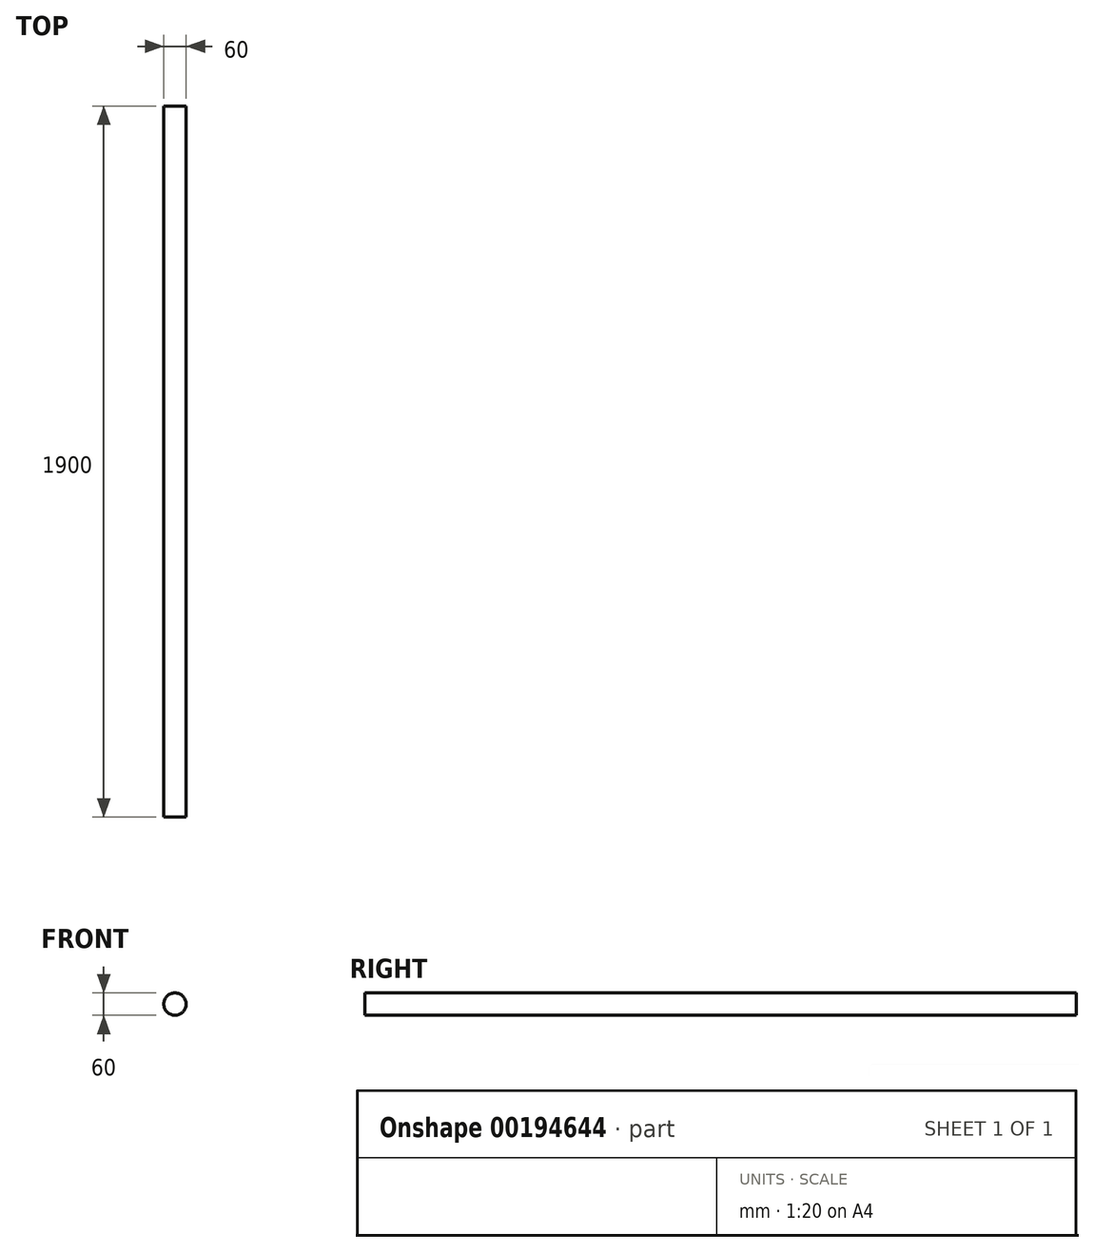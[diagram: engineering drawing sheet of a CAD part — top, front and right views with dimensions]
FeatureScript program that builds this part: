
annotation { "Feature Type Name" : "Feature", "Feature Type Description" : "" }
export const myFeature = defineFeature(function(context is Context, id is Id, definition is map)
    precondition{}
    {
        {
            var Q0;
            Q0=qCreatedBy(makeId("Front.planeOp"),FACE);
            var sketch = newSketch(context, id + "F0", { "sketchPlane" : qUnion([Q0])});
            skCircle(sketch, "E0", {"center": v(0, 0) * mm, "radius": 30 * mm});
            skSolve(sketch);
        }
        {
            var Q0;
            Q0 = qSketchRegion(id + "F0", true);
            var Q1;
            Q1=makeQuery(id+"F0.imprint","IMPRINT",FACE,{"disambiguationData":[TD([[makeQuery(id+"F0.imprint","IMPRINT",EDGE,{"derivedFrom":sQuery(id+"F0.wireOp",EDGE,"E0")}),1.0]])]});
            extrude(context, id + "F1", {"entities" : qUnion([Q0, Q1]), "depth" : 1900 * mm});
        }
    });
